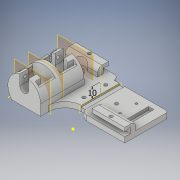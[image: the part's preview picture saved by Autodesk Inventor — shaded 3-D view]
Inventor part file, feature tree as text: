
AUTODESK INVENTOR PART (.ipt)
format: ipt  version: 2018 (Build 220112000, 112)  size: 415,744 bytes
history: native  units: in
note: dims shown in document units (in); Inventor stores cm internally (conversion verified against a paired STEP export)
features: sketch x19, extrude x16, plane x5, fillet x3, mirror x2, other x1, pattern_circular x1
ambient origin geometry x8: Origin, YZ Plane, XZ Plane, XY Plane, X Axis, Y Axis, Z Axis, Center Point
bodies: Solid1 (feature_tree)
feature tree (47):
  extrude  "Extrusion1"  Depth=0.1969in TaperAngle=0.0deg
  extrude  "Extrusion2"  Depth=0.1969in TaperAngle=0.0deg
  plane  "Work Plane1"
  extrude  "Extrusion3"  Depth=0.3937in
  extrude  "Extrusion4"  Depth=0.748in
  extrude  "Extrusion5"  Depth=0.1181in
  plane  "Work Plane2"
  fillet  "Fillet1"  Radius=0.1181in
  mirror  "Mirror1"
  plane  "Work Plane3"
  extrude  "Extrusion6"  Depth=0.1969in TaperAngle=0.0deg
  extrude  "Extrusion7"  Depth=0.0394in
  extrude  "Extrusion8"  Depth=0.1181in TaperAngle=0.0deg
  plane  "Work Plane4"
  sketch  "Sketch9"  dims[d31=-0.689in d32=0.0394in d33=-1.7717in]
  other  "Work Axis1"
  extrude  "Extrusion10"  [1 undecoded]
  mirror  "Mirror4"
  extrude  "Extrusion12"  Depth=0.2953in
  fillet  "Fillet3"  Radius=0.1575in
  sketch  "Sketch15"  dims[d37=0.0in]
  pattern_circular  "Circular Pattern3"  Count=3  [1 undecoded]
  extrude  "Extrusion15"  Depth=0.1181in
  plane  "Work Plane5"
  fillet  "Fillet7"  Radius=0.1181in
  sketch  "Sketch19"  dims[d41=1.1977in d42=0.0984in d43=0.1181in]
  extrude  "Extrusion18"  Depth=0.3937in
  extrude  "Extrusion20"  Depth=0.3937in
  sketch  "Sketch23"  dims[d49=0.1181in d50=0.1181in]
  extrude  "Extrusion21"  Depth=0.1181in
  extrude  "Extrusion22"  Depth=0.1969in TaperAngle=0.0deg
  extrude  "Extrusion23"  Depth=0.3937in
  sketch  "Sketch1"  dims[d6=1.1811in d8=0.1969in d9=0.0in]
  sketch  "Sketch2"  dims[d10=0.1969in d11=1.378in d12=0.0in]
  sketch  "Sketch3"  dims[d13=-0.1969in d14=0.3937in]
  sketch  "Sketch4"  dims[d16=0.374in d17=0.748in]
  sketch  "Sketch5"  dims[d18=0.3937in d19=0.0in d20=0.315in d21=0.1181in]
  sketch  "Sketch6"  dims[d22=0.0787in d23=0.1969in d24=0.0in]
  sketch  "Sketch7"  dims[d25=0.315in d27=0.0394in]
  sketch  "Sketch8"  dims[d28=0.1181in d29=0.1181in d30=0.0in]
  sketch  "Sketch10"  dims[d34=0.3937in d35=0.2953in d36=0.1575in]
  sketch  "Sketch16"  dims[d38=0.1969in d39=1.1811in d40=0.0in]
  sketch  "Sketch20"  dims[d44=0.1969in d45=0.0in d46=0.3937in]
  sketch  "Sketch22"  dims[d47=0.3937in d48=0.7874in]
  sketch  "Sketch24"  dims[d51=0.1181in d52=0.1969in d53=0.0in]
  sketch  "Sketch25"  dims[d54=-1.7717in d55=0.3937in]
  sketch  "Sketch26"  dims[d60=0.0787in d63=0.0984in d64=0.0in d68=0.1969in d69=0.0in d86=0.0787in d87=0.5906in d89=0.1378in d91=0.7874in d92=360.0deg d95=0.5906in d96=0.2953in d97=0.0in d116=0.3937in d117=0.1969in d118=0.3937in d119=0.0in d123=0.3937in d124=0.0in d125=0.1969in d126=0.0591in d127=0.3937in d128=0.0in d130=0.8465in d131=0.1969in d132=0.0787in d133=0.0787in d134=0.5906in d135=0.1181in d136=0.0in d137=0.2362in d138=0.0in d139=0.0in]
note: 2 required parameter values undecoded (feature->parameter linkage not recoverable at this tier; creation-order binding heuristic only, values carry confidence <= 0.55)
